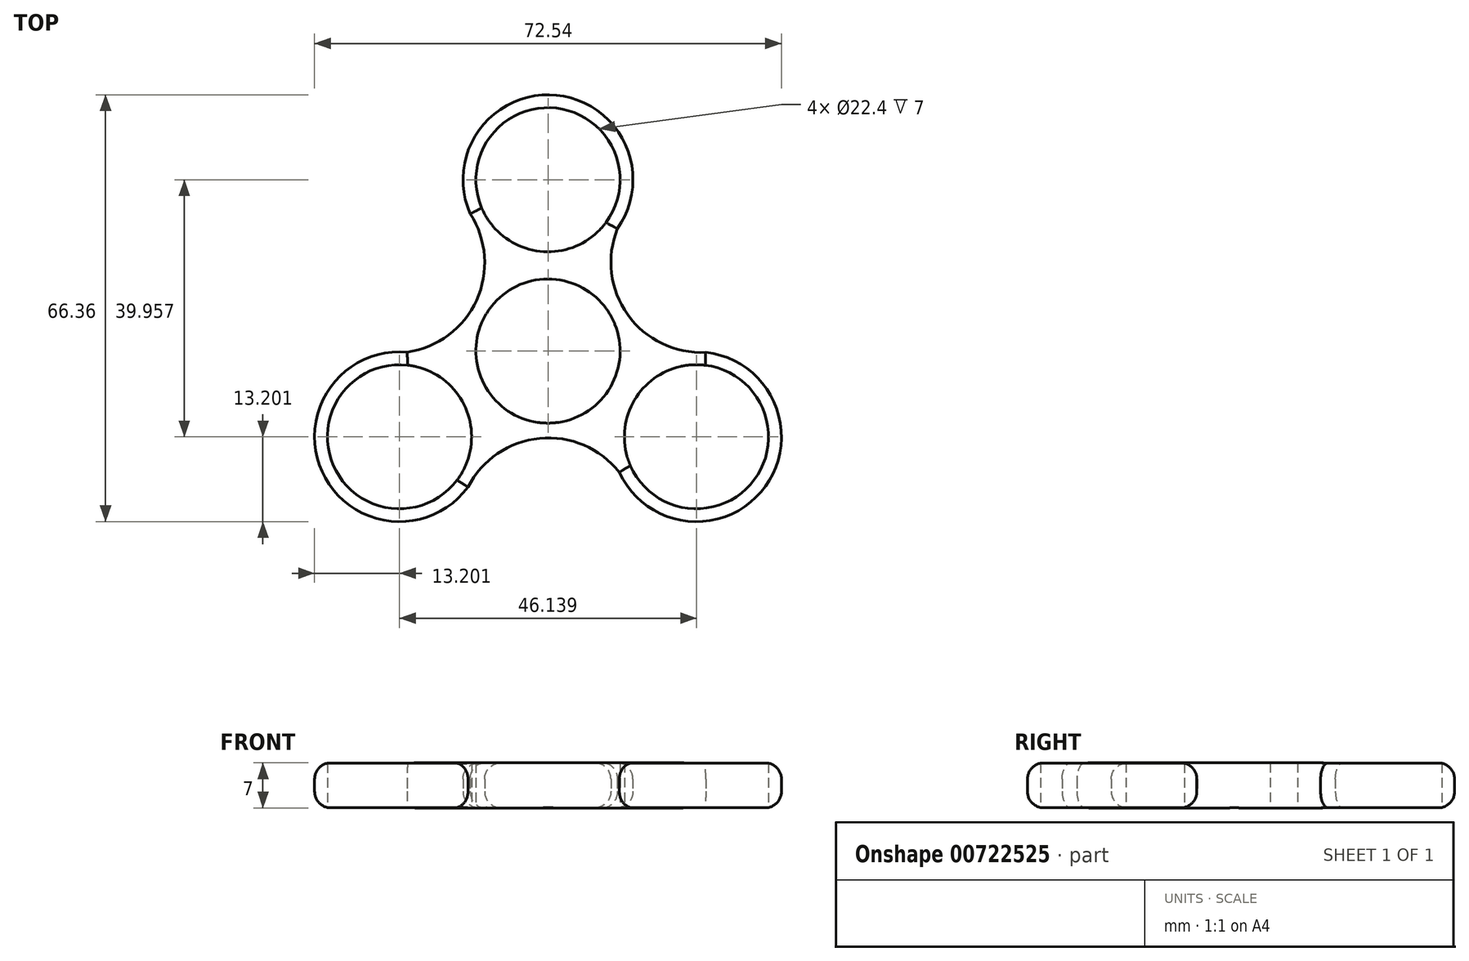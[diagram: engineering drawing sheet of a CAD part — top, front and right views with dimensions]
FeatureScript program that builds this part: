
annotation { "Feature Type Name" : "Feature", "Feature Type Description" : "" }
export const myFeature = defineFeature(function(context is Context, id is Id, definition is map)
    precondition{}
    {
        {
            var Q0;
            Q0=qCreatedBy(makeId("Top.planeOp"),FACE);
            var sketch = newSketch(context, id + "F0", { "sketchPlane" : qUnion([Q0])});
            skCircle(sketch, "E0", {"center": v(0, 0) * mm, "radius": 11.2 * mm});
            skCircle(sketch, "E1", {"center": v(0, 26.64) * mm, "radius": 11.2 * mm});
            skArc(sketch, "E2", {"start": v(10.78, 19.02) * mm, "mid": v(0.24, 39.84) * mm, "end": v(-11.05, 19.43) * mm});
            skCircle(sketch, "E3.1.0", {"center": v(-23.07, -13.32) * mm, "radius": 11.2 * mm});
            skArc(sketch, "E3.1.1", {"start": v(-21.87, -0.17) * mm, "mid": v(-34.62, -19.7) * mm, "end": v(-11.3, -19.29) * mm});
            skCircle(sketch, "E3.2.0", {"center": v(23.07, -13.32) * mm, "radius": 11.2 * mm});
            skArc(sketch, "E3.2.1", {"start": v(11.08, -18.85) * mm, "mid": v(34.38, -20.13) * mm, "end": v(22.35, -0.14) * mm});
            skArc(sketch, "E4", {"start": v(10.78, 19.02) * mm, "mid": v(12.4, 5.66) * mm, "end": v(24.5, -0.2) * mm});
            skArc(sketch, "E5.1.0", {"start": v(-21.87, -0.17) * mm, "mid": v(-11.1, 7.9) * mm, "end": v(-12.08, 21.32) * mm});
            skArc(sketch, "E5.2.0", {"start": v(11.08, -18.85) * mm, "mid": v(-1.3, -13.56) * mm, "end": v(-12.43, -21.13) * mm});
            skSolve(sketch);
        }
        {
            var Q0;
            Q0=makeQuery(id+"F0.imprint","IMPRINT",FACE,{"disambiguationData":[TD([[makeQuery(id+"F0.imprint","IMPRINT",EDGE,{"derivedFrom":sQuery(id+"F0.wireOp",EDGE,"E0")}),-1.0]])]});
            extrude(context, id + "F1", {"entities" : qUnion([Q0]), "depth" : 7 * mm, "offsetDistance" : 25 * mm});
        }
        {
            var Q0;
            Q0=makeQuery(id+"F1.opExtrude","CAP_EDGE",EDGE,{"disambiguationData":[OSD([sQuery(id+"F0.wireOp",EDGE,"E5.2.0")])],"isStart":false});
            var Q1;
            Q1=makeQuery(id+"F1.opExtrude","CAP_EDGE",EDGE,{"disambiguationData":[OSD([sQuery(id+"F0.wireOp",EDGE,"E4")])],"isStart":false});
            var Q2;
            Q2=makeQuery(id+"F1.opExtrude","CAP_EDGE",EDGE,{"disambiguationData":[OSD([sQuery(id+"F0.wireOp",EDGE,"E5.1.0")])],"isStart":false});
            var Q3;
            Q3=makeQuery(id+"F1.opExtrude","CAP_EDGE",EDGE,{"disambiguationData":[OSD([sQuery(id+"F0.wireOp",EDGE,"E3.2.1")])],"isStart":false});
            var Q4;
            Q4=makeQuery(id+"F1.opExtrude","CAP_EDGE",EDGE,{"disambiguationData":[OSD([sQuery(id+"F0.wireOp",EDGE,"E2")])],"isStart":false});
            var Q5;
            Q5=makeQuery(id+"F1.opExtrude","CAP_EDGE",EDGE,{"disambiguationData":[OSD([sQuery(id+"F0.wireOp",EDGE,"E3.1.1")])],"isStart":false});
            fillet(context, id + "F2", {"entities" : qUnion([Q0, Q1, Q2, Q3, Q4, Q5]), "radius" : 2.5 * mm, "tangentPropagation" : true, "allowEdgeOverflow" : false});
        }
        {
            var Q0;
            Q0=makeQuery(id+"F1.opExtrude","CAP_EDGE",EDGE,{"disambiguationData":[OSD([sQuery(id+"F0.wireOp",EDGE,"E5.1.0")])],"isStart":true});
            var Q1;
            Q1=makeQuery(id+"F1.opExtrude","CAP_EDGE",EDGE,{"disambiguationData":[OSD([sQuery(id+"F0.wireOp",EDGE,"E4")])],"isStart":true});
            var Q2;
            Q2=makeQuery(id+"F1.opExtrude","CAP_EDGE",EDGE,{"disambiguationData":[OSD([sQuery(id+"F0.wireOp",EDGE,"E5.2.0")])],"isStart":true});
            var Q3;
            Q3=makeQuery(id+"F1.opExtrude","CAP_EDGE",EDGE,{"disambiguationData":[OSD([sQuery(id+"F0.wireOp",EDGE,"E3.1.1")])],"isStart":true});
            var Q4;
            Q4=makeQuery(id+"F1.opExtrude","CAP_EDGE",EDGE,{"disambiguationData":[OSD([sQuery(id+"F0.wireOp",EDGE,"E2")])],"isStart":true});
            var Q5;
            Q5=makeQuery(id+"F1.opExtrude","CAP_EDGE",EDGE,{"disambiguationData":[OSD([sQuery(id+"F0.wireOp",EDGE,"E3.2.1")])],"isStart":true});
            fillet(context, id + "F3", {"entities" : qUnion([Q0, Q1, Q2, Q3, Q4, Q5]), "radius" : 2.55 * mm, "tangentPropagation" : true, "allowEdgeOverflow" : false});
        }
    });
